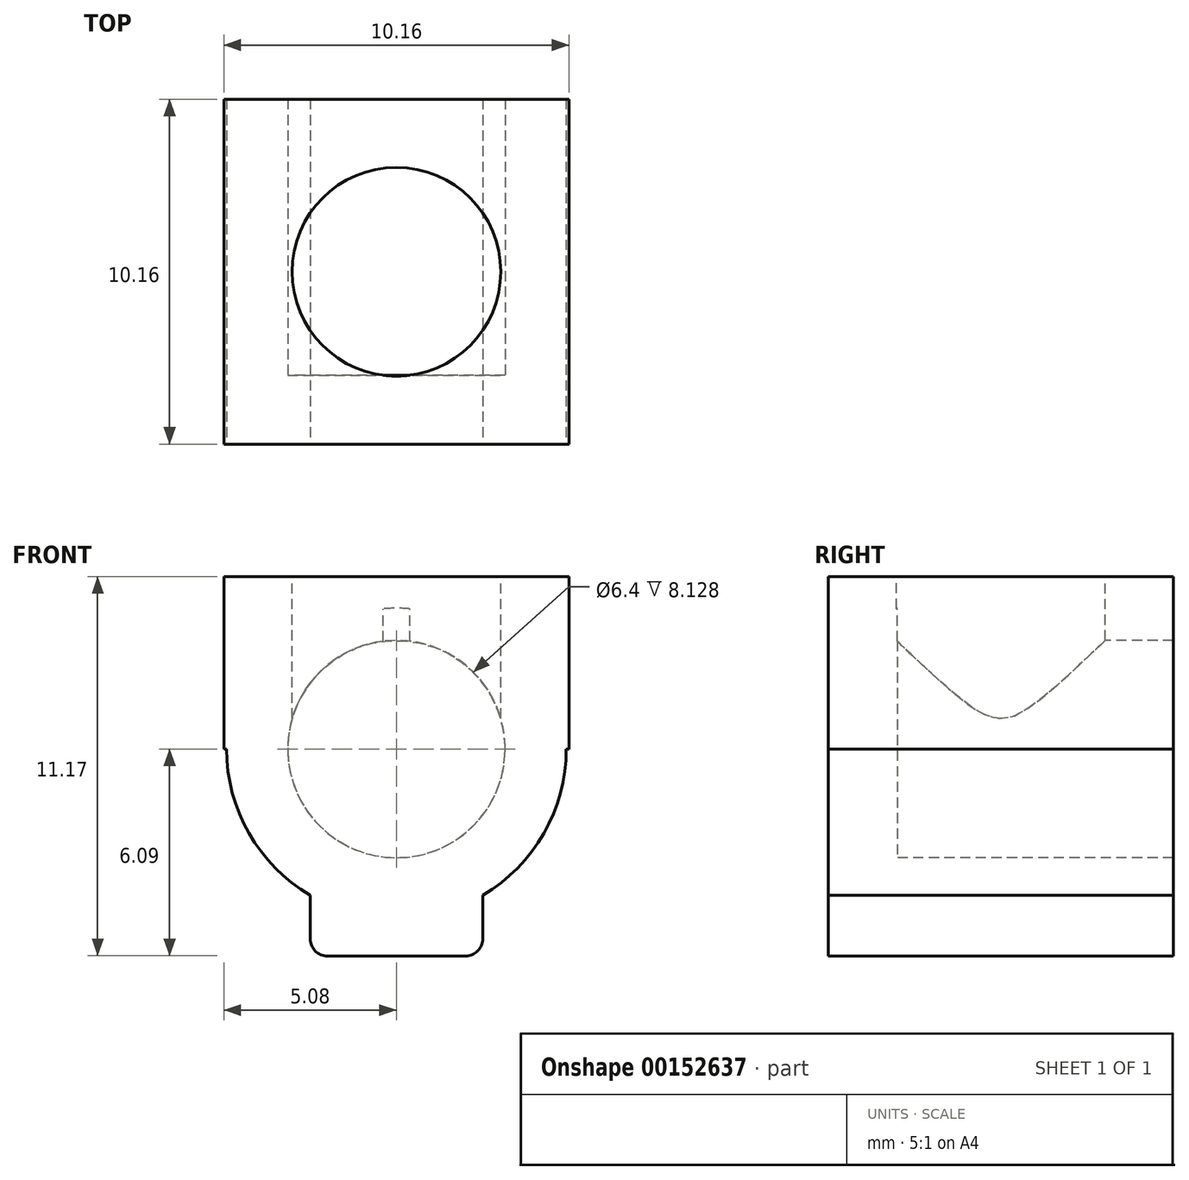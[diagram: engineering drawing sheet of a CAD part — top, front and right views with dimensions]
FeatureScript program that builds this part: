
annotation { "Feature Type Name" : "Feature", "Feature Type Description" : "" }
export const myFeature = defineFeature(function(context is Context, id is Id, definition is map)
    precondition{}
    {
        {
            var Q0;
            Q0=qCreatedBy(makeId("Top.planeOp"),FACE);
            var sketch = newSketch(context, id + "F0", { "sketchPlane" : qUnion([Q0])});
            skLineSegment(sketch, "E0", {"start": v(0, 34.64) * mm, "end": v(-30, -17.32) * mm, "construction": true});
            skLineSegment(sketch, "E1", {"start": v(-30, -17.32) * mm, "end": v(30, -17.32) * mm, "construction": true});
            skLineSegment(sketch, "E2", {"start": v(30, -17.32) * mm, "end": v(0, 34.64) * mm, "construction": true});
            skLineSegment(sketch, "E3", {"start": v(0, 34.64) * mm, "end": v(0, 0) * mm, "construction": true});
            skLineSegment(sketch, "E4", {"start": v(0, 0) * mm, "end": v(30, -17.32) * mm, "construction": true});
            skLineSegment(sketch, "E5", {"start": v(0, 0) * mm, "end": v(-30, -17.32) * mm, "construction": true});
            skSolve(sketch);
        }
        {
            var Q0;
            Q0=qCreatedBy(makeId("Front.planeOp"),FACE);
            var sketch = newSketch(context, id + "F1", { "sketchPlane" : qUnion([Q0])});
            skCircle(sketch, "E6", {"center": v(0, 0) * mm, "radius": 5 * mm});
            skSolve(sketch);
        }
        {
            var Q0;
            Q0=qSketchRegion(id+"F1",true);
            extrude(context, id + "F2", {"entities" : qUnion([Q0]), "oppositeDirection" : true, "depth" : 34.64 * mm});
        }
        {
            var Q0;
            Q0=makeQuery(id+"F2.opExtrude","CAP_FACE",FACE,{"disambiguationData":[OSD([sQuery(id+"F1.wireOp",EDGE,"E6")])],"isStart":true});
            var sketch = newSketch(context, id + "F3", { "sketchPlane" : qUnion([Q0])});
            skLineSegment(sketch, "E7.bottom", {"start": v(-2.54, -3.2) * mm, "end": v(2.54, -3.2) * mm});
            skLineSegment(sketch, "E7.top", {"start": v(-2.54, -6.1) * mm, "end": v(2.54, -6.1) * mm});
            skLineSegment(sketch, "E7.left", {"start": v(-2.54, -3.2) * mm, "end": v(-2.54, -6.1) * mm});
            skLineSegment(sketch, "E7.right", {"start": v(2.54, -3.2) * mm, "end": v(2.54, -6.1) * mm});
            skSolve(sketch);
        }
        {
            var Q0;
            Q0=qSketchRegion(id+"F3",true);
            var Q1;
            Q1=makeQuery(id+"F2.opExtrude","CAP_FACE",FACE,{"disambiguationData":[OSD([sQuery(id+"F1.wireOp",EDGE,"E6")])],"isStart":false});
            extrude(context, id + "F4", {"entities" : qUnion([Q0]), "operationType" : NewBodyOperationType.ADD, "endBound" : BoundingType.UP_TO_SURFACE, "oppositeDirection" : true, "endBoundEntityFace" : qUnion([Q1]), "depth" : 25.4 * mm});
        }
        {
            var Q0;
            Q0=makeQuery(id+"F2.opExtrude","CAP_FACE",FACE,{"disambiguationData":[OSD([sQuery(id+"F1.wireOp",EDGE,"E6")])],"isStart":true});
            var sketch = newSketch(context, id + "F5", { "sketchPlane" : qUnion([Q0])});
            skCircle(sketch, "E8", {"center": v(0, 0) * mm, "radius": 3.2 * mm});
            skSolve(sketch);
        }
        {
            var Q0;
            Q0=qCreatedBy(makeId("Right.planeOp"),FACE);
            var sketch = newSketch(context, id + "F6", { "sketchPlane" : qUnion([Q0])});
            skLineSegment(sketch, "E9.bottom", {"start": v(33.88, 10.16) * mm, "end": v(31.34, 10.16) * mm});
            skLineSegment(sketch, "E9.top", {"start": v(33.88, 2.54) * mm, "end": v(31.34, 2.54) * mm});
            skLineSegment(sketch, "E9.left", {"start": v(33.88, 10.16) * mm, "end": v(33.88, 2.54) * mm});
            skLineSegment(sketch, "E9.right", {"start": v(31.34, 10.16) * mm, "end": v(31.34, 2.54) * mm});
            skLineSegment(sketch, "E10.bottom", {"start": v(26.26, 10.16) * mm, "end": v(23.72, 10.16) * mm});
            skLineSegment(sketch, "E10.top", {"start": v(26.26, 2.54) * mm, "end": v(23.72, 2.54) * mm});
            skLineSegment(sketch, "E10.left", {"start": v(26.26, 10.16) * mm, "end": v(26.26, 2.54) * mm});
            skLineSegment(sketch, "E10.right", {"start": v(23.72, 10.16) * mm, "end": v(23.72, 2.54) * mm});
            skSolve(sketch);
        }
        {
            var Q0;
            Q0=qSketchRegion(id+"F6",true);
            extrude(context, id + "F7", {"entities" : qUnion([Q0]), "operationType" : NewBodyOperationType.ADD, "depth" : 3.8 * mm, "hasSecondDirection" : true, "secondDirectionOppositeDirection" : true, "secondDirectionDepth" : 3.8 * mm});
        }
        {
            var Q0;
            Q0=makeQuery(id+"F7.opExtrude","SWEPT_EDGE",EDGE,{"disambiguationData":[OSD([sQuery(id+"F6.wireOp",EDGE,"E10.bottom"),sQuery(id+"F6.wireOp",EDGE,"E10.left")])]});
            var Q1;
            Q1=makeQuery(id+"F7.opExtrude","SWEPT_EDGE",EDGE,{"disambiguationData":[OSD([sQuery(id+"F6.wireOp",EDGE,"E9.bottom"),sQuery(id+"F6.wireOp",EDGE,"E9.right")])]});
            var Q2;
            Q2=makeQuery(id+"F7.opExtrude","SWEPT_EDGE",EDGE,{"disambiguationData":[OSD([sQuery(id+"F6.wireOp",EDGE,"E9.bottom"),sQuery(id+"F6.wireOp",EDGE,"E9.left")])]});
            var Q3;
            Q3=makeQuery(id+"F7.opExtrude","SWEPT_EDGE",EDGE,{"disambiguationData":[OSD([sQuery(id+"F6.wireOp",EDGE,"E10.bottom"),sQuery(id+"F6.wireOp",EDGE,"E10.right")])]});
            var Q4;
            Q4=makeQuery(id+"F7.opExtrude","CAP_EDGE",EDGE,{"disambiguationData":[OSD([sQuery(id+"F6.wireOp",EDGE,"E10.left")])],"isStart":true});
            var Q5;
            Q5=makeQuery(id+"F7.opExtrude","CAP_EDGE",EDGE,{"disambiguationData":[OSD([sQuery(id+"F6.wireOp",EDGE,"E10.right")])],"isStart":true});
            var Q6;
            Q6=makeQuery(id+"F7.opExtrude","CAP_EDGE",EDGE,{"disambiguationData":[OSD([sQuery(id+"F6.wireOp",EDGE,"E10.bottom")])],"isStart":true});
            var Q7;
            Q7=makeQuery(id+"F7.opExtrude","CAP_EDGE",EDGE,{"disambiguationData":[OSD([sQuery(id+"F6.wireOp",EDGE,"E9.right")])],"isStart":true});
            var Q8;
            Q8=makeQuery(id+"F7.opExtrude","CAP_EDGE",EDGE,{"disambiguationData":[OSD([sQuery(id+"F6.wireOp",EDGE,"E9.bottom")])],"isStart":true});
            var Q9;
            Q9=makeQuery(id+"F7.opExtrude","CAP_EDGE",EDGE,{"disambiguationData":[OSD([sQuery(id+"F6.wireOp",EDGE,"E9.left")])],"isStart":true});
            var Q10;
            Q10=makeQuery(id+"F7.opExtrude","CAP_EDGE",EDGE,{"disambiguationData":[OSD([sQuery(id+"F6.wireOp",EDGE,"E10.bottom")])],"isStart":false});
            var Q11;
            Q11=makeQuery(id+"F7.opExtrude","CAP_EDGE",EDGE,{"disambiguationData":[OSD([sQuery(id+"F6.wireOp",EDGE,"E10.left")])],"isStart":false});
            var Q12;
            Q12=makeQuery(id+"F7.opExtrude","CAP_EDGE",EDGE,{"disambiguationData":[OSD([sQuery(id+"F6.wireOp",EDGE,"E10.right")])],"isStart":false});
            var Q13;
            Q13=makeQuery(id+"F7.opExtrude","CAP_EDGE",EDGE,{"disambiguationData":[OSD([sQuery(id+"F6.wireOp",EDGE,"E9.right")])],"isStart":false});
            var Q14;
            Q14=makeQuery(id+"F7.opExtrude","CAP_EDGE",EDGE,{"disambiguationData":[OSD([sQuery(id+"F6.wireOp",EDGE,"E9.bottom")])],"isStart":false});
            var Q15;
            Q15=makeQuery(id+"F7.opExtrude","CAP_EDGE",EDGE,{"disambiguationData":[OSD([sQuery(id+"F6.wireOp",EDGE,"E9.left")])],"isStart":false});
            fillet(context, id + "F8", {"entities" : qUnion([Q0, Q1, Q2, Q3, Q4, Q5, Q6, Q7, Q8, Q9, Q10, Q11, Q12, Q13, Q14, Q15]), "radius" : 0.76 * mm, "tangentPropagation" : true, "allowEdgeOverflow" : false});
        }
        {
            var Q0;
            Q0=makeQuery(id+"F4.opExtrude","SWEPT_EDGE",EDGE,{"disambiguationData":[OSD([sQuery(id+"F3.wireOp",EDGE,"E7.top"),sQuery(id+"F3.wireOp",EDGE,"E7.left")])]});
            var Q1;
            Q1=makeQuery(id+"F4.opExtrude","SWEPT_EDGE",EDGE,{"disambiguationData":[OSD([sQuery(id+"F3.wireOp",EDGE,"E7.top"),sQuery(id+"F3.wireOp",EDGE,"E7.left")])]});
            var Q2;
            Q2=makeQuery(id+"F4.opExtrude","SWEPT_EDGE",EDGE,{"disambiguationData":[OSD([sQuery(id+"F3.wireOp",EDGE,"E7.top"),sQuery(id+"F3.wireOp",EDGE,"E7.right")])]});
            var Q3;
            Q3=makeQuery(id+"F4.opExtrude","SWEPT_EDGE",EDGE,{"disambiguationData":[OSD([sQuery(id+"F3.wireOp",EDGE,"E7.top"),sQuery(id+"F3.wireOp",EDGE,"E7.right")])]});
            fillet(context, id + "F9", {"entities" : qUnion([Q0, Q1, Q2, Q3]), "radius" : 0.5 * mm, "tangentPropagation" : true, "allowEdgeOverflow" : false});
        }
        {
            var Q0;
            Q0=makeQuery(id+"F4.boolean.opBoolean","MERGE",FACE,{"derivedFrom":[makeQuery(id+"F2.opExtrude","CAP_FACE",FACE,{"disambiguationData":[OSD([sQuery(id+"F1.wireOp",EDGE,"E6")])],"isStart":true}),makeQuery(id+"F4.opExtrude","CAP_FACE",FACE,{"disambiguationData":[OSD([sQuery(id+"F3.wireOp",EDGE,"E7.bottom"),sQuery(id+"F3.wireOp",EDGE,"E7.top"),sQuery(id+"F3.wireOp",EDGE,"E7.left"),sQuery(id+"F3.wireOp",EDGE,"E7.right")])],"isStart":true})]});
            var sketch = newSketch(context, id + "F10", { "sketchPlane" : qUnion([Q0])});
            skCircle(sketch, "E11", {"center": v(0, 0) * mm, "radius": 4.83 * mm});
            skSolve(sketch);
        }
        {
            var Q0;
            Q0 = qSketchRegion(id + "F10", true);
            extrude(context, id + "F11", {"entities" : qUnion([Q0]), "operationType" : NewBodyOperationType.ADD, "oppositeDirection" : true, "depth" : 2.03 * mm});
        }
        {
            var Q0;
            Q0=qCreatedBy(makeId("Top.planeOp"),FACE);
            var sketch = newSketch(context, id + "F12", { "sketchPlane" : qUnion([Q0])});
            skLineSegment(sketch, "E12.bottom", {"start": v(-5.08, 0) * mm, "end": v(5.08, 0) * mm});
            skLineSegment(sketch, "E12.top", {"start": v(-5.08, 10.16) * mm, "end": v(5.08, 10.16) * mm});
            skLineSegment(sketch, "E12.left", {"start": v(-5.08, 0) * mm, "end": v(-5.08, 10.16) * mm});
            skLineSegment(sketch, "E12.right", {"start": v(5.08, 0) * mm, "end": v(5.08, 10.16) * mm});
            skSolve(sketch);
        }
        {
            var Q0;
            Q0 = qSketchRegion(id + "F12", true);
            extrude(context, id + "F13", {"entities" : qUnion([Q0]), "operationType" : NewBodyOperationType.ADD, "depth" : 5.08 * mm});
        }
        {
            var Q0;
            Q0=makeQuery(id+"F13.opExtrude","CAP_FACE",FACE,{"disambiguationData":[OSD([sQuery(id+"F12.wireOp",EDGE,"E12.bottom"),sQuery(id+"F12.wireOp",EDGE,"E12.top"),sQuery(id+"F12.wireOp",EDGE,"E12.left"),sQuery(id+"F12.wireOp",EDGE,"E12.right")])],"isStart":false});
            var sketch = newSketch(context, id + "F14", { "sketchPlane" : qUnion([Q0])});
            skCircle(sketch, "E13", {"center": v(0, 5.08) * mm, "radius": 3.07 * mm});
            skPoint(sketch, "E13.centerSnap0", {"position": v(-5.08, 5.08) * mm});
            skSolve(sketch);
        }
        {
            var Q0;
            Q0 = qSketchRegion(id + "F14", true);
            extrude(context, id + "F15", {"entities" : qUnion([Q0]), "operationType" : NewBodyOperationType.REMOVE, "oppositeDirection" : true, "depth" : 5.08 * mm});
        }
        {
            var Q0;
            Q0=qCreatedBy(makeId("Top.planeOp"),FACE);
            var sketch = newSketch(context, id + "F16", { "sketchPlane" : qUnion([Q0])});
            skLineSegment(sketch, "E14.bottom", {"start": v(-5.08, 34.64) * mm, "end": v(5.08, 34.64) * mm});
            skLineSegment(sketch, "E14.top", {"start": v(-5.08, 24.48) * mm, "end": v(5.08, 24.48) * mm});
            skLineSegment(sketch, "E14.left", {"start": v(-5.08, 34.64) * mm, "end": v(-5.08, 24.48) * mm});
            skLineSegment(sketch, "E14.right", {"start": v(5.08, 34.64) * mm, "end": v(5.08, 24.48) * mm});
            skSolve(sketch);
        }
        {
            var Q0;
            Q0 = qSketchRegion(id + "F16", true);
            var Q1;
            Q1=makeQuery(id+"F4.opExtrude","SWEPT_FACE",FACE,{"disambiguationData":[OSD([sQuery(id+"F3.wireOp",EDGE,"E7.top")])]});
            extrude(context, id + "F17", {"entities" : qUnion([Q0]), "operationType" : NewBodyOperationType.ADD, "endBound" : BoundingType.UP_TO_SURFACE, "oppositeDirection" : true, "endBoundEntityFace" : qUnion([Q1]), "depth" : 25.4 * mm});
        }
        {
            var Q0;
            Q0=makeQuery(id+"F17.boolean.opBoolean","MERGE",FACE,{"derivedFrom":[makeQuery(id+"F4.opExtrude","SWEPT_FACE",FACE,{"disambiguationData":[OSD([sQuery(id+"F3.wireOp",EDGE,"E7.top")])]}),makeQuery(id+"F17.opExtrude","CAP_FACE",FACE,{"disambiguationData":[OSD([sQuery(id+"F16.wireOp",EDGE,"E14.bottom"),sQuery(id+"F16.wireOp",EDGE,"E14.top"),sQuery(id+"F16.wireOp",EDGE,"E14.left"),sQuery(id+"F16.wireOp",EDGE,"E14.right")])],"isStart":false})]});
            var sketch = newSketch(context, id + "F18", { "sketchPlane" : qUnion([Q0])});
            skCircle(sketch, "E15", {"center": v(0, -29.56) * mm, "radius": 3.81 * mm});
            skPoint(sketch, "E15.centerSnap0", {"position": v(0, -34.64) * mm});
            skPoint(sketch, "E15.centerSnap1", {"position": v(-5.08, -29.56) * mm});
            skSolve(sketch);
        }
        {
            var Q0;
            Q0 = qSketchRegion(id + "F18", true);
            extrude(context, id + "F19", {"entities" : qUnion([Q0]), "operationType" : NewBodyOperationType.REMOVE, "oppositeDirection" : true, "depth" : 8.9 * mm});
        }
        {
            var Q0;
            Q0=makeQuery(id+"F5.imprint","IMPRINT",FACE,{"disambiguationData":[TD([[makeQuery(id+"F5.imprint","IMPRINT",EDGE,{"derivedFrom":sQuery(id+"F5.wireOp",EDGE,"E8")}),1.0]])]});
            extrude(context, id + "F20", {"entities" : qUnion([Q0]), "operationType" : NewBodyOperationType.REMOVE, "oppositeDirection" : true, "depth" : 31.75 * mm});
        }
        {
            var Q0;
            Q0=makeQuery(id+"F19.boolean.opBoolean","COPY",EDGE,{"derivedFrom":makeQuery(id+"F19.opExtrude","CAP_EDGE",EDGE,{"disambiguationData":[OSD([sQuery(id+"F18.wireOp",EDGE,"E15")])],"isStart":false})});
            fillet(context, id + "F21", {"entities" : qUnion([Q0]), "radius" : 1.27 * mm, "tangentPropagation" : true, "allowEdgeOverflow" : false});
        }
        {
            var Q0;
            Q0=makeQuery(id+"F17.opExtrude","SWEPT_FACE",FACE,{"disambiguationData":[OSD([sQuery(id+"F16.wireOp",EDGE,"E14.left")])]});
            var sketch = newSketch(context, id + "F22", { "sketchPlane" : qUnion([Q0])});
            skLineSegment(sketch, "E16.bottom", {"start": v(-34.64, -6.1) * mm, "end": v(-10.16, -6.1) * mm});
            skLineSegment(sketch, "E16.top", {"start": v(-34.64, 16.6) * mm, "end": v(-10.16, 16.6) * mm});
            skLineSegment(sketch, "E16.left", {"start": v(-34.64, -6.1) * mm, "end": v(-34.64, 16.6) * mm});
            skLineSegment(sketch, "E16.right", {"start": v(-10.16, -6.1) * mm, "end": v(-10.16, 16.6) * mm});
            skSolve(sketch);
        }
        {
            var Q0;
            Q0 = qSketchRegion(id + "F22", true);
            extrude(context, id + "F23", {"entities" : qUnion([Q0]), "operationType" : NewBodyOperationType.REMOVE, "oppositeDirection" : true, "depth" : 25.4 * mm});
        }
        {
            var Q0;
            Q0=makeQuery(id+"F13.boolean.opBoolean","MERGE",FACE,{"derivedFrom":[makeQuery(id+"F4.boolean.opBoolean","MERGE",FACE,{"derivedFrom":[makeQuery(id+"F2.opExtrude","CAP_FACE",FACE,{"disambiguationData":[OSD([sQuery(id+"F1.wireOp",EDGE,"E6")])],"isStart":true}),makeQuery(id+"F4.opExtrude","CAP_FACE",FACE,{"disambiguationData":[OSD([sQuery(id+"F3.wireOp",EDGE,"E7.bottom"),sQuery(id+"F3.wireOp",EDGE,"E7.top"),sQuery(id+"F3.wireOp",EDGE,"E7.left"),sQuery(id+"F3.wireOp",EDGE,"E7.right")])],"isStart":true})]}),makeQuery(id+"F13.opExtrude","SWEPT_FACE",FACE,{"disambiguationData":[OSD([sQuery(id+"F12.wireOp",EDGE,"E12.bottom")])]})]});
            var sketch = newSketch(context, id + "F24", { "sketchPlane" : qUnion([Q0])});
            skCircle(sketch, "E17", {"center": v(0, 0) * mm, "radius": 4.15 * mm});
            skSolve(sketch);
        }
        {
            var Q0;
            Q0 = qSketchRegion(id + "F24", true);
            extrude(context, id + "F25", {"entities" : qUnion([Q0]), "operationType" : NewBodyOperationType.ADD, "oppositeDirection" : true, "depth" : 2.03 * mm});
        }
    });
